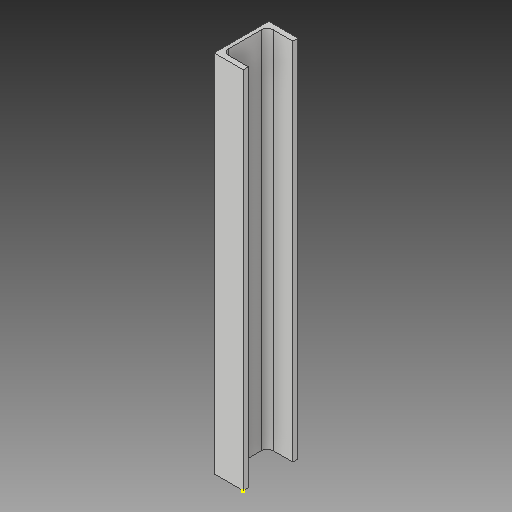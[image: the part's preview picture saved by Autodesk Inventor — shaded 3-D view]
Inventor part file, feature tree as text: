
AUTODESK INVENTOR PART (.ipt)
format: ipt  version: 2019 (Build 230136000, 136)  size: 94,208 bytes
history: native  units: mm
features: sketch x2, extrude x1
ambient origin geometry x8: Origin, YZ Plane, XZ Plane, XY Plane, X Axis, Y Axis, Z Axis, Center Point
bodies: Solid1 (feature_tree)
feature tree (3):
  sketch  "Sketch1"  dims[d0=40.0mm d1=75.0mm]
  extrude  "Extrusion1"  Depth=75.0mm
  sketch  "Sketch2"  dims[d2=40.0mm d3=7.0mm d5=35.0mm d6=61.0mm d7=8.0mm d8=500.0mm d9=0.0mm]
